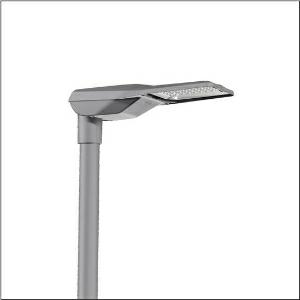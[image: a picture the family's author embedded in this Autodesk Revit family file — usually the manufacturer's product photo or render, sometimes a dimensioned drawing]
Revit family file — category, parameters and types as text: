
# Revit family: streetlight_sl_21_iq_mini___p0_8ab_5xe2r31g08gb_8bc5
name_source: partatom
category: Lighting Fixtures
units: mm (PartAtom-declared; Revit-internal decimal feet)

## family parameters
Cut with Voids When Loaded = No
Host = Face
Light Source = No
Part Type = Normal
Room Calculation Point = No
Round Connector Dimension = Use Diameter
Shared = No

## types (1)
- --- (1 x LED, 4930 lm, 37.1 W, 3000K)
    Apparent Load = 37 VA
    CIE Flux Codes = 36 71 98 100 100
    Color Rendering = 70
    Color Temperature = 3000K
    Default Elevation = 1800 mm
    Description = Streetlight SL 21 iQ mini, mast luminaire, primary light control with lens, of PMMA, primary optical cover: cover, of toughened safety glass, transparent, light distribution: P0.8aB, light emission: direct distribution, primary light characteristic: asymmetric, installation type: post-top, side-entry, LED, High Power LED, rated luminous flux: 4.930lm, luminous efficacy: 133lm/W, light colour: 730, colour temperature: 3000K, control gear: iQ Street-Remote, control: pre-setting: linear dimming characteristic, Street-Remote, Auto-Match, Temp-Guard, Lumen-Switch, Night-Set, Smart-Wire, Light-Fading, Desk-Remote (wireless, voltage-free reading and setting of iQ features in the workshop via application-optimized NFC function/RFID function), optimised constant luminous flux control (CLO 2.0), mains connection: 220..240V, AC, 50/60Hz, start of lifetime: 37W, end of service life: 39W, reduction: 18W, luminaire housing, of diecast aluminium, powder-coated, SITECO metallic grey (DB 702S), corrosivity category C5 high according to DIN EN ISO 12944, please order mast flange separately, inclination adjustable: 0°, 5°, 10°, 15°, sealing non-destructively replaceable, multi-level sealing system, length: 628mm, width: 235mm, height: 110mm, mast flange for spigot size: 42mm (side-entry): 5XC10008XM4, 60/48mm (side-entry/post-top): 5XC10108XM2, 76/60mm (side-entry/post-top): 5XC10108XM1, mounting height: 4..8m, protection rating (complete): IP66, insulation class (complete): insulation class II (safety insulation), certification: CE, ENEC, ENEC+, VDE, impact resistance: IK10, permissible operating ambient temperature for outdoor applications: -40..+50°C, standard-compliant lighting for roads and squares, packaging unit: 1 piece

Light Distribution: P0.8aB
    Height = 110 mm
    Lamp = 1 x LED
    Lamp Light Flux = 4930 lm
    Lamp Power = 37.1 W
    Lamp count = 1
    Length = 625 mm
    Luminous efficacy = 133 lm/W
    Manufacturer = Siteco
    ModVariant = No
    Model = 5XE2R31G08GB
    Number of Poles = 1
    OnlyDefault = Yes
    Power Factor = 1
    Product Name = Streetlight SL 21 iQ mini | P0.8aB
    Product group = mast luminaire | pylon top
    ProductGroupID = 6100
    Protection Class = Protection class II
    Protection Degree = IP 66
    RLX_Detail_Level = 1
    RLX_Emergency_Light_Flux = 0 lm
    RLX_Emergency_Type = 0
    RLX_Emergency_Type_DB = No
    RlxData = <blob elided: 91945 chars, md5=75acd04a>
    Socket = socket
    Standby Power = 0 W
    System Light Flux = 4930 lm
    System Power = 37 W
    Type Comments = factory setting: luminous flux: 100 % | dim-lin: 254 | 385 mA
    Type Image = l_1003519.jpg
    URL = http://relux.com
    VarID = @adj_082263
    Voltage = 0 V
    Weight = 0.00 kg
    Width = 234 mm

## geometry (parser evidence)
native form markers: Blend x4, Sweep x11
no freeform markers — native parametric forms only
